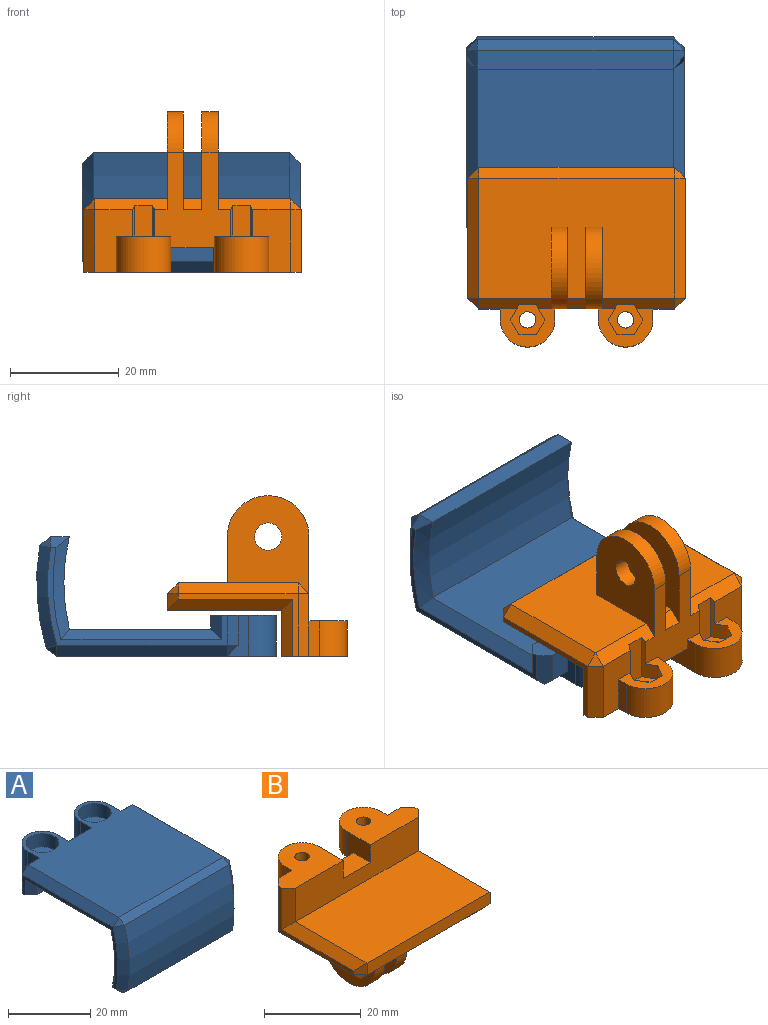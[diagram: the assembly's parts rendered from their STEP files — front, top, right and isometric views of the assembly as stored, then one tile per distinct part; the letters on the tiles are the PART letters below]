
ASSEMBLY  parts=2 mates=2
PART A: 51 faces, bbox 40x44x22.5 mm
  f0: cylinder r=1.5mm len=3.5mm, axis (0,0,1), area 33mm2, adj f48,f50
  f1: cylinder r=1.5mm len=3.5mm, axis (0,0,1), area 33mm2, adj f46,f49
  f2: plane 5.5x4mm, normal (0,1,0), area 22mm2, adj f7,f14,f29,f50
  f3: plane 5.5x4mm, normal (0,1,0), area 22mm2, adj f9,f15,f17,f49
  f4: plane 14x2.5mm, normal (0,-1,0), area 35mm2, adj f10,f11,f24,f49
  f5: plane 14x2.5mm, normal (0,-1,0), area 35mm2, adj f8,f12,f24,f50
  f6: plane 33x18mm, normal (1,0,0), area 53.1mm2, adj f9,f10,f36,f39,f41,f42,f44,f49
  f7: plane 5.5x2mm, normal (-0.71,0.71,0), area 15.6mm2, adj f2,f25,f26,f50
  f8: plane 4.5x2mm, normal (-0.71,-0.71,0), area 9.9mm2, adj f5,f25,f27,f50
  f9: plane 5.5x2mm, normal (0.71,0.71,0), area 15.6mm2, adj f3,f6,f32,f49
  f10: plane 4.5x2mm, normal (0.71,-0.71,0), area 9.9mm2, adj f4,f6,f39,f49
  f11: plane 7.5x7mm, normal (-1,0,0), area 29.5mm2, adj f4,f16,f18,f19,f20,f24,f49
  f12: plane 7.5x7mm, normal (1,0,0), area 29.5mm2, adj f5,f13,f18,f19,f20,f24,f50
  f13: cylinder r=5mm len=10mm, axis (0,0,1), area 117.8mm2, adj f12,f14,f20,f50
  f14: plane 7.5x4mm, normal (-1,0,0), area 17mm2, adj f2,f13,f20,f29,f50
  f15: plane 7.5x4mm, normal (1,0,0), area 17mm2, adj f3,f16,f17,f20,f49
  f16: cylinder r=5mm len=10mm, axis (0,0,1), area 117.8mm2, adj f11,f15,f20,f49
  f17: plane 4x2mm, normal (0,0.71,0.71), area 11.3mm2, adj f3,f15,f20,f32
  f18: plane 8x3mm, normal (0,1,0), area 24mm2, adj f11,f12,f19,f24
  f19: plane 8x2mm, normal (0,0.71,0.71), area 22.6mm2, adj f11,f12,f18,f20
  f20: plane 40.29x36mm, normal (0,0,1), area 1184.6mm2, adj f11,f12,f13,f14,f15,f16,f17,f19
  f21: cylinder r=41.62mm len=36mm, axis (-1,0,0), area 688.2mm2, adj f34,f35,f40,f41
  f22: plane 36x3.46mm, normal (0,0,-1), area 124.7mm2, adj f23,f33,f40,f44
  f23: cylinder r=36.62mm len=36mm, axis (-1,0,0), area 617.6mm2, adj f22,f24,f30,f42
  f24: plane 36x31mm, normal (0,0,-1), area 976mm2, adj f4,f5,f11,f12,f18,f23,f27,f39
  f25: plane 33x18mm, normal (-1,0,0), area 53.1mm2, adj f7,f8,f27,f28,f30,f33,f34,f50
  f26: plane 2x2mm, normal (-0.58,0.58,0.58), area 3.5mm2, adj f7,f28,f29
  f27: plane 29.55x2mm, normal (-0.71,0,-0.71), area 78.6mm2, adj f8,f24,f25,f30
  f28: plane 31.29x2mm, normal (-0.71,0,0.71), area 88.5mm2, adj f20,f25,f26,f31
  f29: plane 4x2mm, normal (0,0.71,0.71), area 11.3mm2, adj f2,f14,f20,f26
  f30: cone r=38.62mm half-angle=45deg, axis (-1,0,0), area 48.5mm2, adj f23,f25,f27,f33
  f31: plane 2x2mm, normal (-0.63,-0.46,0.63), area 3.1mm2, adj f28,f34,f35
  f32: plane 2x2mm, normal (0.58,0.58,0.58), area 3.5mm2, adj f9,f17,f36
  f33: plane 3.46x2mm, normal (-0.71,0,-0.71), area 6.3mm2, adj f22,f25,f30,f37
  f34: cone r=41.62mm half-angle=45deg, axis (1,0,0), area 52.8mm2, adj f21,f25,f31,f37
  f35: plane 36x1.91mm, normal (0,-0.6,0.8), area 85.8mm2, adj f20,f21,f31,f38
  f36: plane 31.29x2mm, normal (0.71,0,0.71), area 88.5mm2, adj f6,f20,f32,f38
  f37: plane 2x2mm, normal (-0.61,-0.51,-0.61), area 3.3mm2, adj f33,f34,f40
  f38: plane 2x2mm, normal (0.63,-0.46,0.63), area 3.1mm2, adj f35,f36,f41
  f39: plane 29.55x2mm, normal (0.71,0,-0.71), area 78.6mm2, adj f6,f10,f24,f42
  f40: plane 36x1.97mm, normal (0,-0.65,-0.76), area 93.1mm2, adj f21,f22,f37,f43
  f41: cone r=39.62mm half-angle=45deg, axis (-1,0,0), area 52.8mm2, adj f6,f21,f38,f43
  f42: cone r=36.62mm half-angle=45deg, axis (1,0,0), area 48.5mm2, adj f6,f23,f39,f44
  f43: plane 2x2mm, normal (0.61,-0.51,-0.61), area 3.3mm2, adj f40,f41,f44
  f44: plane 3.46x2mm, normal (0.71,0,-0.71), area 6.3mm2, adj f6,f22,f42,f43
  f45: cylinder r=4mm len=8mm, axis (0,0,1), area 100.5mm2, adj f20,f46
  f46: plane 8x8mm, normal (0,0,1), area 43.2mm2, adj f1,f45
  f47: cylinder r=4mm len=8mm, axis (0,0,1), area 100.5mm2, adj f20,f48
  f48: plane 8x8mm, normal (0,0,1), area 43.2mm2, adj f0,f47
  f49: plane 16x12mm, normal (0,0,-1), area 128.2mm2, adj f1,f3,f4,f6,f9,f10,f11,f15
  f50: plane 16x12mm, normal (0,0,-1), area 128.2mm2, adj f0,f2,f5,f7,f8,f12,f13,f14
PART B: 64 faces, bbox 40x33x29.5 mm
  f0: plane 13.3x2mm, normal (0,0.71,-0.71), area 33.8mm2, adj f4,f6,f13,f21,f27,f29,f46,f58
  f1: plane 3.4x2mm, normal (0,0.71,-0.71), area 9.6mm2, adj f6,f29,f55,f57
  f2: plane 36x2mm, normal (0,-0.71,-0.71), area 101.8mm2, adj f3,f6,f7,f8
  f3: plane 2x2mm, normal (-0.58,-0.58,-0.58), area 3.5mm2, adj f2,f18,f19
  f4: plane 8.75x3.18mm, normal (0,1,0), area 27.8mm2, adj f0,f13,f21,f48
  f5: plane 8.75x3.18mm, normal (0,1,0), area 27.8mm2, adj f11,f20,f22,f50
  f6: plane 36x22mm, normal (0,0,-1), area 714mm2, adj f0,f1,f2,f19,f22,f23,f54,f55
  f7: plane 36x3mm, normal (0,-1,0), area 108mm2, adj f2,f17,f18,f24
  f8: plane 2x2mm, normal (0.58,-0.58,-0.58), area 3.5mm2, adj f2,f23,f24
  f9: plane 3.18x3mm, normal (0,-1,0), area 9.5mm2, adj f10,f12,f31,f50
  f10: plane 3x2.75mm, normal (-0.87,-0.5,0), area 9.5mm2, adj f9,f11,f31,f50
  f11: plane 8.75x2.75mm, normal (-0.87,0.5,0), area 14.2mm2, adj f5,f10,f22,f29,f31,f50
  f12: plane 3x2.75mm, normal (0.87,-0.5,0), area 9.5mm2, adj f9,f20,f31,f50
  f13: plane 8.75x2.75mm, normal (0.87,0.5,0), area 14.2mm2, adj f0,f4,f14,f29,f32,f48
  f14: plane 3x2.75mm, normal (0.87,-0.5,0), area 9.5mm2, adj f13,f15,f32,f48
  f15: plane 3.18x3mm, normal (0,-1,0), area 9.5mm2, adj f14,f16,f32,f48
  f16: plane 3x2.75mm, normal (-0.87,-0.5,0), area 9.5mm2, adj f15,f21,f32,f48
  f17: plane 36x21mm, normal (0,0,1), area 756mm2, adj f7,f26,f28,f47
  f18: plane 3x2mm, normal (-0.71,-0.71,0), area 5.7mm2, adj f3,f7,f26,f39
  f19: plane 22x2mm, normal (-0.71,0,-0.71), area 62.2mm2, adj f3,f6,f25,f39
  f20: plane 8.75x2.75mm, normal (0.87,0.5,0), area 14.2mm2, adj f5,f12,f22,f31,f38,f50
  f21: plane 8.75x2.75mm, normal (-0.87,0.5,0), area 14.2mm2, adj f0,f4,f16,f32,f46,f48
  f22: plane 13.3x2mm, normal (0,0.71,-0.71), area 33.8mm2, adj f5,f6,f11,f20,f25,f29,f38,f54
  f23: plane 22x2mm, normal (0.71,0,-0.71), area 62.2mm2, adj f6,f8,f27,f45
  f24: plane 3x2mm, normal (0.71,-0.71,0), area 5.7mm2, adj f7,f8,f28,f45
  f25: plane 2x2mm, normal (-0.58,0.58,-0.58), area 3.5mm2, adj f19,f22,f34
  f26: plane 23x2mm, normal (-0.71,0,0.71), area 59.4mm2, adj f17,f18,f33,f39
  f27: plane 2x2mm, normal (0.58,0.58,-0.58), area 3.5mm2, adj f0,f23,f43
  f28: plane 23x2mm, normal (0.71,0,0.71), area 59.4mm2, adj f17,f24,f44,f45
  f29: plane 17.5x13.96mm, normal (0,1,0), area 148.8mm2, adj f0,f1,f11,f13,f22,f30,f31,f32
  f30: plane 8x5mm, normal (0,0,1), area 40mm2, adj f29,f37,f42,f47
  f31: plane 10x7mm, normal (0,0,-1), area 35.8mm2, adj f9,f10,f11,f12,f20,f29,f35,f36
  f32: plane 10x7mm, normal (0,0,-1), area 35.8mm2, adj f13,f14,f15,f16,f21,f29,f40,f41
  f33: plane 10.5x2mm, normal (-0.71,-0.71,0), area 26.9mm2, adj f26,f39,f47,f53
  f34: plane 11.5x2mm, normal (-0.71,0.71,0), area 32.5mm2, adj f25,f38,f39,f53
  f35: plane 6.5x2mm, normal (-1,0,0), area 13mm2, adj f31,f36,f38,f53
  f36: cylinder r=5mm len=10mm, axis (0,0,1), area 102.1mm2, adj f31,f35,f37,f53
  f37: plane 7x6.5mm, normal (1,0,0), area 35.5mm2, adj f29,f30,f31,f36,f47,f53
  f38: plane 11.5x6.98mm, normal (0,1,0), area 60.9mm2, adj f20,f22,f31,f34,f35,f53
  f39: plane 22x11.5mm, normal (-1,0,0), area 32.5mm2, adj f18,f19,f26,f33,f34,f53
  f40: cylinder r=5mm len=10mm, axis (0,0,1), area 102.1mm2, adj f32,f41,f42,f52
  f41: plane 6.5x2mm, normal (1,0,0), area 13mm2, adj f32,f40,f46,f52
  f42: plane 7x6.5mm, normal (-1,0,0), area 35.5mm2, adj f29,f30,f32,f40,f47,f52
  f43: plane 11.5x2mm, normal (0.71,0.71,0), area 32.5mm2, adj f27,f45,f46,f52
  f44: plane 10.5x2mm, normal (0.71,-0.71,0), area 26.9mm2, adj f28,f45,f47,f52
  f45: plane 22x11.5mm, normal (1,0,0), area 32.5mm2, adj f23,f24,f28,f43,f44,f52
  f46: plane 11.5x6.98mm, normal (0,1,0), area 60.9mm2, adj f0,f21,f32,f41,f43,f52
  f47: plane 36x8.5mm, normal (0,-1,0), area 270mm2, adj f17,f30,f33,f37,f42,f44,f52,f53
  f48: plane 6.35x5.5mm, normal (0,0,-1), area 19.1mm2, adj f4,f13,f14,f15,f16,f21,f49
  f49: cylinder r=1.5mm len=3.5mm, axis (0,0,1), area 33mm2, adj f48,f52
  f50: plane 6.35x5.5mm, normal (0,0,-1), area 19.1mm2, adj f5,f9,f10,f11,f12,f20,f51
  f51: cylinder r=1.5mm len=3.5mm, axis (0,0,1), area 33mm2, adj f50,f53
  f52: plane 16x12mm, normal (0,0,1), area 128.2mm2, adj f40,f41,f42,f43,f44,f45,f46,f47
  f53: plane 16x12mm, normal (0,0,1), area 128.2mm2, adj f33,f34,f35,f36,f37,f38,f39,f47
  f54: plane 18x15mm, normal (-1,0,0), area 198.2mm2, adj f6,f22,f29,f56,f61,f63
  f55: plane 18x15mm, normal (1,0,0), area 198.2mm2, adj f1,f6,f29,f56,f61,f63
  f56: plane 8.5x3mm, normal (0,-1,0), area 25.5mm2, adj f6,f54,f55,f63
  f57: plane 18x15mm, normal (-1,0,0), area 198.2mm2, adj f1,f6,f29,f59,f60,f62
  f58: plane 18x15mm, normal (1,0,0), area 198.2mm2, adj f0,f6,f29,f59,f60,f62
  f59: plane 8.5x3mm, normal (0,-1,0), area 25.5mm2, adj f6,f57,f58,f62
  f60: cylinder r=2.5mm len=5mm, axis (-1,0,0), area 47.1mm2, adj f57,f58
  f61: cylinder r=2.5mm len=5mm, axis (-1,0,0), area 47.1mm2, adj f54,f55
  f62: cylinder r=7.5mm len=15mm, axis (1,0,0), area 70.7mm2, adj f29,f57,f58,f59
  f63: cylinder r=7.5mm len=15mm, axis (1,0,0), area 70.7mm2, adj f29,f54,f55,f56
PLACE A rot(axis=(1,0,0),180deg) t=(0,-11.68,13.5)mm
PLACE B rot(axis=(1,0,0),180deg) t=(0.22,-24.71,5)mm
MATE parallel B.f7 <-> A.f18  axis (0,1,0) through (0.22,-3.71,10)mm
MATE planar B.f36 <-> A.f20  axis (0,0,-1) through (-8.78,-31.71,0)mm
